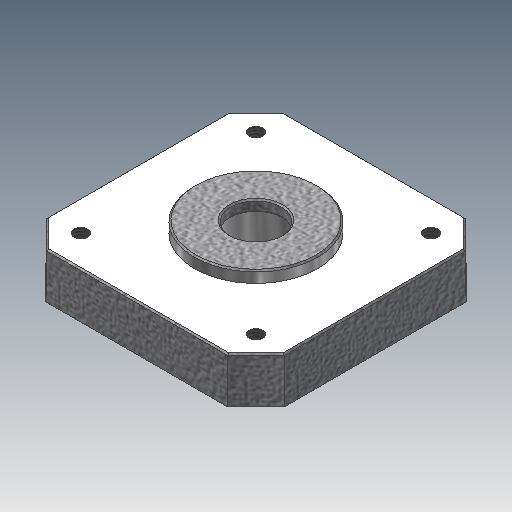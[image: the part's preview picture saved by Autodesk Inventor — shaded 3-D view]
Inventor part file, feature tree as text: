
AUTODESK INVENTOR PART (.ipt)
format: ipt  version: 2020.2 (Build 242310000, 310)  size: 279,552 bytes
history: native  units: mm
features: sketch x8, extrude x6, chamfer x3, hole x2, projected_geometry x1
ambient origin geometry x8: Origin, YZ Plane, XZ Plane, XY Plane, X Axis, Y Axis, Z Axis, Center Point
bodies: Body1 (feature_tree)
feature tree (20):
  extrude  "Extrusion7"  Depth=5.0mm
  extrude  "Extrusion8"  Depth=5.0mm
  extrude  "Extrusion9"  Depth=5.0mm
  extrude  "Extrusion10"  Depth=5.0mm
  extrude  "Extrusion11"  Depth=8.0mm
  hole  "Hole5"  [1 undecoded]
  extrude  "Extrusion12"  Depth=39.0mm
  hole  "Hole6"  [1 undecoded]
  chamfer  "Chamfer1"  Distance=16.0mm
  chamfer  "Chamfer2"  Distance=8.25mm
  chamfer  "Chamfer3"  Distance=12.0mm
  sketch  "Sketch11"  dims[d82=42.0mm d83=5.0mm]
  sketch  "Sketch12"  dims[d84=5.0mm d85=5.0mm]
  sketch  "Sketch13"  dims[d86=5.0mm d87=5.0mm]
  sketch  "Sketch14"  dims[d88=5.0mm d89=5.0mm]
  projected_geometry  "Projected Loop3"
  sketch  "Sketch15"  dims[d90=5.0mm d91=8.0mm d92=0.174533mm]
  sketch  "Sketch16"  dims[d93=21.8mm d94=2.0mm d95=0.0mm]
  sketch  "Sketch17"  dims[d96=26.0mm d97=39.0mm]
  sketch  "Sketch18"  dims[d98=6.0mm d99=0.0mm d100=1.0mm d101=0.0mm d102=16.0mm d103=8.25mm d104=0.0mm d105=9.0mm d106=6.0mm d107=6.3mm d108=2.0mm d109=90.0deg d110=12.0mm d111=20.594885mm d112=12.0mm d113=0.75mm d114=0.0mm d115=31.0mm d116=2.459mm d117=6.0mm d118=6.3mm d119=2.0mm d120=90.0deg d121=8.8mm d122=20.594885mm d124=31.0mm d125=0.25mm d126=1.0mm d127=45.0deg d128=0.25mm d129=1.0mm d130=45.0deg d131=1.0mm d132=2.0mm d133=45.0deg]
note: 2 required parameter values undecoded (feature->parameter linkage not recoverable at this tier; creation-order binding heuristic only, values carry confidence <= 0.55)
